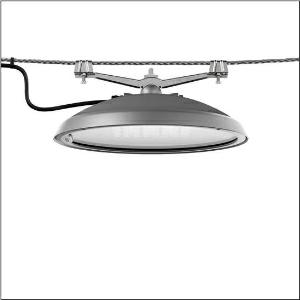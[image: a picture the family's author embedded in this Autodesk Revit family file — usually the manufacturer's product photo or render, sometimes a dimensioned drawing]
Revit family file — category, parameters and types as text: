
# Revit family: dl_r__50_iq_mini___p1_0s_5xa248u41f08fe_3d02
name_source: partatom
category: Lighting Fixtures
units: mm (PartAtom-declared; Revit-internal decimal feet)

## family parameters
Cut with Voids When Loaded = No
Host = Face
Light Source = No
Part Type = Normal
Room Calculation Point = No
Round Connector Dimension = Use Diameter
Shared = No

## types (1)
- --- (1 x LED, 2610 lm, 15.7 W, 4000K)
    Apparent Load = 16 VA
    CIE Flux Codes = 23 54 93 100 100
    Color Rendering = 70
    Color Temperature = 4000K
    Default Elevation = 1800 mm
    Description = DL® 50 iQ mini, catenary luminaire, primary light control with lens, of PMMA, primary optical cover: cover, of toughened safety glass, transparent, light distribution: P1.0s, light emission: direct distribution, primary light characteristic: symmetric, installation type: suspended mounting, LED, High Power LED, rated luminous flux: 2.610lm, luminous efficacy: 166lm/W, light colour: 740, colour temperature: 4000K, control: optimised constant luminous flux control (CLO 2.0), Desk-Remote (wireless, voltage-free reading and setting of iQ features in the workshop via application-optimized NFC function/RFID function), Light-Fading, Smart-Wire, Night-Set, Lumen-Switch, Temp-Guard, Auto-Match, Street-Remote, mains connection: 230..240V, AC, 50/60Hz, start of lifetime: 16W, end of service life: 16W, reduction: 8W, luminaire housing, of diecast aluminium, powder-coated, Siteco® metallic grey (DB 702S), diameter: 500mm, height: 115mm, protection rating (complete): IP66, insulation class (complete): insulation class II (safety insulation), certification: CE, ENEC, VDE, impact resistance: IK08, permissible operating ambient temperature for outdoor applications: -25..+40°C, standard-compliant lighting for roads and squares, packaging unit: 1 piece

Light Distribution: P1.0s
    Height = 124 mm  [stored 0.406824 ft]
    Lamp = 1 x LED
    Lamp Light Flux = 2610 lm
    Lamp Power = 15.7 W
    Lamp count = 1
    Length = 500 mm
    Luminous efficacy = 166 lm/W
    Manufacturer = Siteco
    ModVariant = No
    Model = 5XA248U41F08FE
    Number of Poles = 1
    OnlyDefault = Yes
    Power Factor = 1
    Product Name = DL® 50 iQ mini | P1.0s
    Product group = catenary luminaire
    ProductGroupID = 6300
    Protection Class = Protection class II
    Protection Degree = IP 66
    RLX_Detail_Level = 1
    RLX_Emergency_Light_Flux = 0 lm
    RLX_Emergency_Type = 0
    RLX_Emergency_Type_DB = No
    RlxData = <blob elided: 123505 chars, md5=1089b58b>
    Socket = socket
    Standby Power = 0 W
    System Light Flux = 2610 lm
    System Power = 16 W
    Type Comments = factory setting: luminous flux: 100 % | dim-lin: 254 | 319 mA
    Type Image = l_1242791.jpg
    URL = http://relux.com
    VarID = @adj_087129
    Voltage = 0 V
    Weight = 0.00 kg
    Width = 0 mm  [stored 0 ft]

note: [stored X ft] marks values corroborated as IEEE doubles in the binary element streams (Revit-internal decimal feet)

## geometry (parser evidence)
native form markers: Blend x4, Sweep x12
no freeform markers — native parametric forms only
